# Revit family: BE_50891.6_de_DE
name_source: partatom
category: Lighting Fixtures
units: mm (PartAtom-declared; Revit-internal decimal feet)

## family parameters
Cut with Voids When Loaded = Yes
Host = Face
Light Source = No
Part Type = Normal
Room Calculation Point = Yes
Round Connector Dimension = Use Diameter
Shared = No

## types (1)
- BEGA_50891.6_K3
    AC/DC = AC
    Aktualisierung = 2022-11-30T04:00:03
    Apparent Load = 0 VA
    BEGA_Dummy = No
    BEGA_IES = Yes
    BEGA_Intern = Yes
    BEGA_Intern_Konstruktion = Yes
    BEGA_Intern_an = Yes
    BEGA_Intern_aus = Yes
    Beschreibung_Sonderanfertigung = Hier können Sie Informationen zur Sonderanfertigung eintragen.
    Bestellnummer = 50891.6K3
    CE_Konformität = ja
    Default Elevation = 0 mm  [stored 0 ft]
    Description = Ringkrone
    ENEC = ja
    Energieeffizienzklasse = LED A++ - A
    Farbtemperatur = 3000 K
    Farbwiedergabeindex = CRI > 90
    Frequenz = 50-60 Hz
    Gewicht = 43.6 kg
    LED_Modulbezeichnung = 24x LED-0800/930
    Lamp = LED 388.8 W
    Lampenlichtstrom = 30120 lm
    Lastklassifizierung = Beleuchtung
    Lebensdauerkriterien = L70B50 @ 25 °C = 195000 h
    Leuchtenlichtstrom = 19368 lm
    Logo = BEGA_Logo.png
    Manufacturer = BEGA
    Material_09 = BEGA_glass_clear
    Material_12 = BEGA_Kunststoff_klar
    Material_15 = BEGA_lighting_medium_matt
    Material_17 = BEGA_reflector
    Material_19 = BEGA_Dummy_matt
    Material_23 = BEGA_Oberfläche_Chrom_poliert
    Material_28 = BEGA_Oberfläche_Kupfer_gefaerbt_matt
    Material_35 = BEGA_Oberfläche_Samtschwarz_matt
    Model = 50891.6K3
    Produktdatenblatt = https://cdn.bega.com
    Schutzart = IP 20
    Schutzklasse = I
    Sonderanfertigung = No
    Spannung = 240 V
    URL = https://www.bega.com
    Umgebungstemperatur = 25 °C

note: [stored X ft] marks values corroborated as IEEE doubles in the binary element streams (Revit-internal decimal feet)

## geometry (parser evidence)
native form markers: Blend x9, Sweep x2
no freeform markers — native parametric forms only
